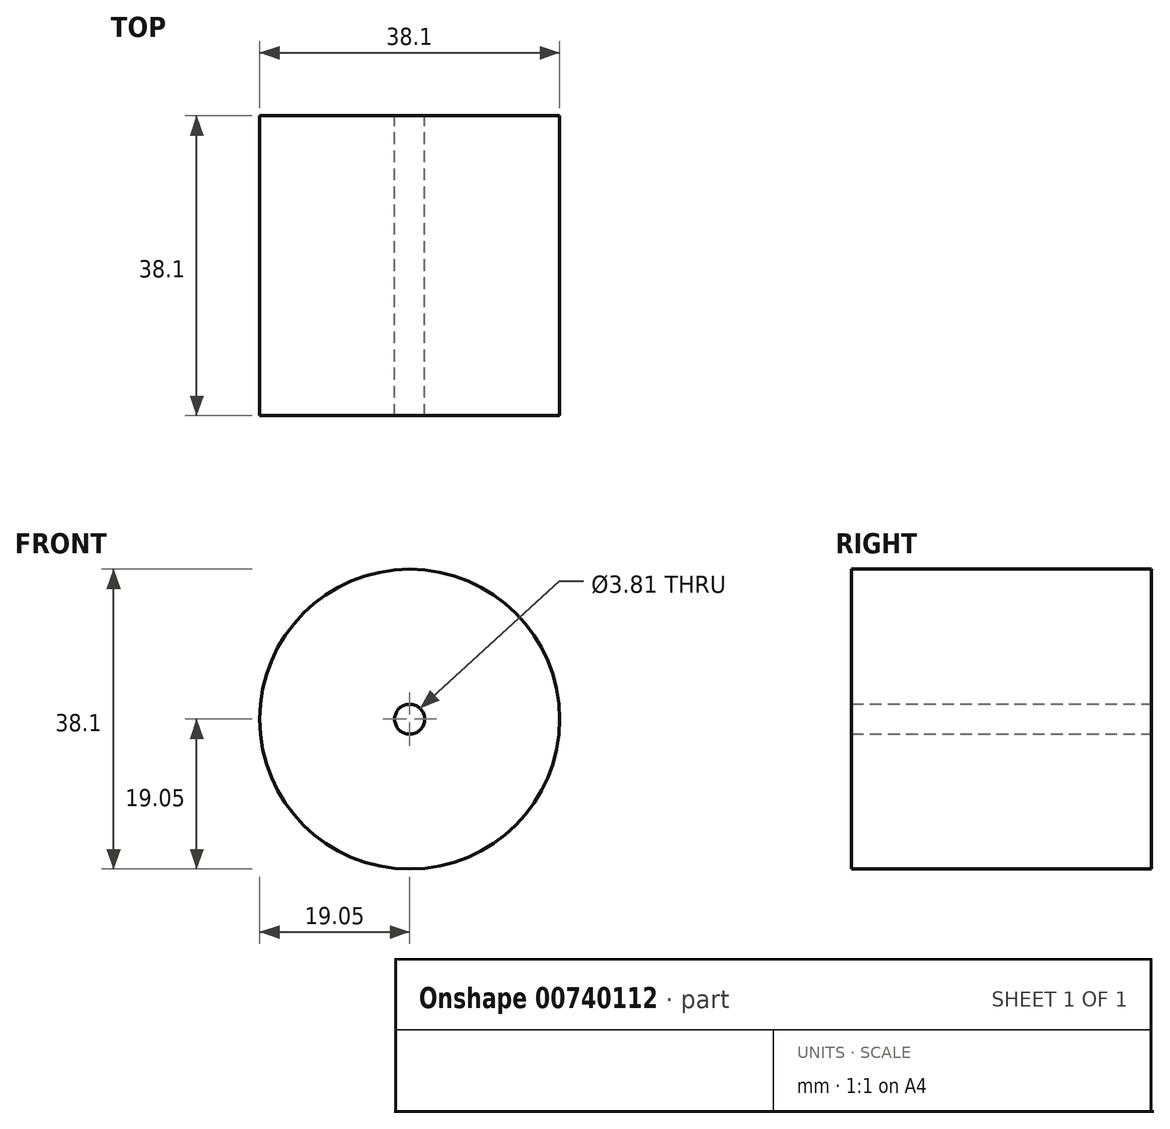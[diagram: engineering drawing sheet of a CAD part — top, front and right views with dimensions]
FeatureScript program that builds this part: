
annotation { "Feature Type Name" : "Feature", "Feature Type Description" : "" }
export const myFeature = defineFeature(function(context is Context, id is Id, definition is map)
    precondition{}
    {
        {
            var Q0;
            Q0=qCreatedBy(makeId("Front.planeOp"),FACE);
            var sketch = newSketch(context, id + "F0", { "sketchPlane" : qUnion([Q0])});
            skCircle(sketch, "E0", {"center": v(0, 0) * mm, "radius": 19.05 * mm});
            skCircle(sketch, "E1", {"center": v(0, 0) * mm, "radius": 16.51 * mm});
            skCircle(sketch, "E2", {"center": v(0, 0) * mm, "radius": 1.9 * mm});
            skSolve(sketch);
        }
        {
            var Q0;
            Q0=makeQuery(id+"F0.imprint","IMPRINT",FACE,{"disambiguationData":[TD([[makeQuery(id+"F0.imprint","IMPRINT",EDGE,{"derivedFrom":sQuery(id+"F0.wireOp",EDGE,"E1")}),1.0]])]});
            var Q1;
            Q1=makeQuery(id+"F0.imprint","IMPRINT",FACE,{"disambiguationData":[TD([[makeQuery(id+"F0.imprint","IMPRINT",EDGE,{"derivedFrom":sQuery(id+"F0.wireOp",EDGE,"E0")}),1.0]])]});
            extrude(context, id + "F1", {"entities" : qUnion([Q0, Q1]), "depth" : 38.1 * mm, "offsetDistance" : 25.4 * mm});
        }
    });
